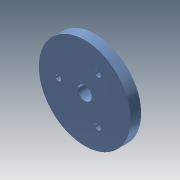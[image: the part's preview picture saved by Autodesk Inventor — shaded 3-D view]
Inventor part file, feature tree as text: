
AUTODESK INVENTOR PART (.ipt)
format: ipt  version: 2015 (Build 190159000, 159)  size: 110,080 bytes
history: native  units: mm
features: sketch x4, extrude x3
ambient origin geometry x8: Origin, YZ Plane, XZ Plane, XY Plane, X Axis, Y Axis, Z Axis, Center Point
bodies: Solid1 (feature_tree)
feature tree (7):
  extrude  "Extrusion1"  Depth=5.0mm
  extrude  "Extrusion2"  Depth=3.8mm
  extrude  "Extrusion3"  Depth=3.0mm
  sketch  "Sketch4"  dims[d9=3.8mm d10=0.0mm d11=2.0mm d12=2.0mm d13=2.0mm d14=3.8mm d15=0.0mm]
  sketch  "Sketch1"  dims[d0=33.15mm d1=5.0mm]
  sketch  "Sketch2"  dims[d2=3.8mm d3=0.0mm d4=3.0mm]
  sketch  "Sketch3"  dims[d7=3.0mm d8=3.0mm]
